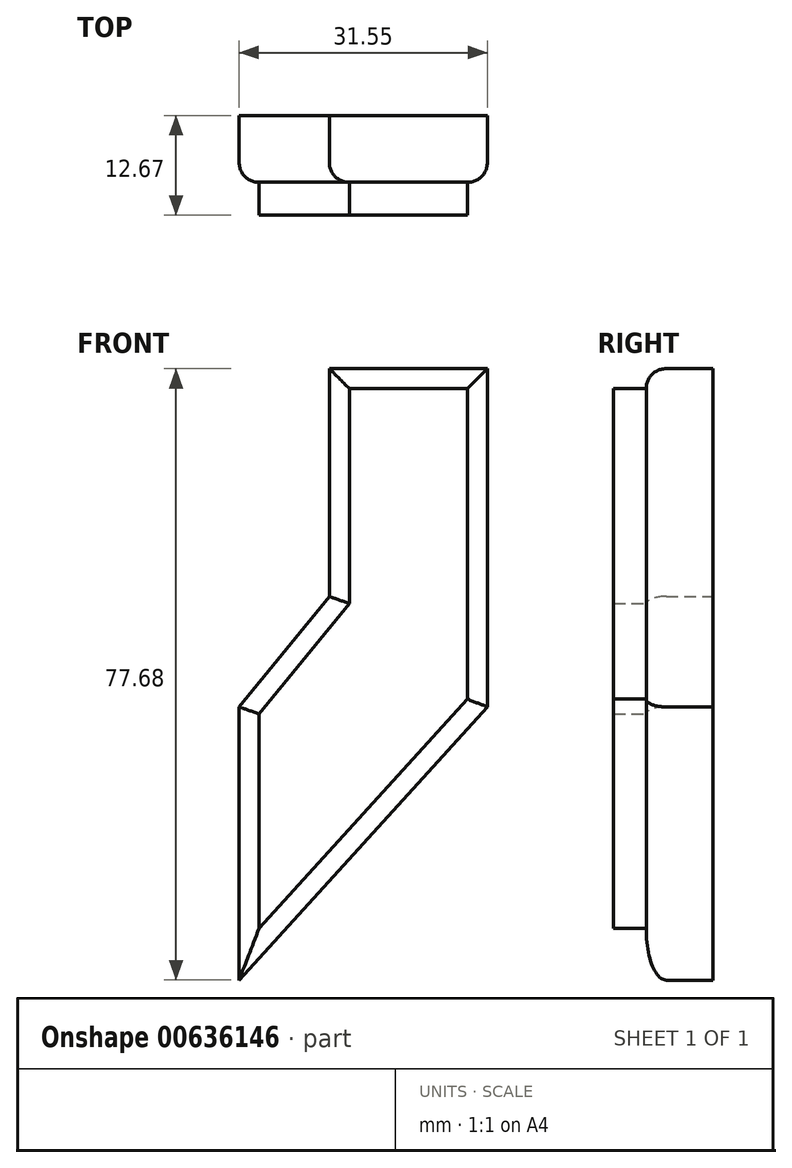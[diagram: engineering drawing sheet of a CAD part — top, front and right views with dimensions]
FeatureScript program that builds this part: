
annotation { "Feature Type Name" : "Feature", "Feature Type Description" : "" }
export const myFeature = defineFeature(function(context is Context, id is Id, definition is map)
    precondition{}
    {
        {
            var Q0;
            Q0=qCreatedBy(makeId("Front.planeOp"),FACE);
            var sketch = newSketch(context, id + "F0", { "sketchPlane" : qUnion([Q0])});
            skLineSegment(sketch, "E0", {"start": v(13.94, 0) * mm, "end": v(25.4, 14.03) * mm});
            skLineSegment(sketch, "E1", {"start": v(25.4, 14.03) * mm, "end": v(25.4, 42.97) * mm});
            skLineSegment(sketch, "E2", {"start": v(25.4, 42.97) * mm, "end": v(45.49, 42.97) * mm});
            skLineSegment(sketch, "E3", {"start": v(45.49, 42.97) * mm, "end": v(45.49, 0) * mm});
            skLineSegment(sketch, "E4", {"start": v(45.49, 0) * mm, "end": v(13.94, -34.71) * mm});
            skLineSegment(sketch, "E5", {"start": v(13.94, -34.71) * mm, "end": v(13.94, 0) * mm});
            skSolve(sketch);
        }
        {
            var Q0;
            Q0=makeQuery(id+"F0.imprint","IMPRINT",FACE,{"disambiguationData":[TD([[makeQuery(id+"F0.imprint","IMPRINT",EDGE,{"derivedFrom":sQuery(id+"F0.wireOp",EDGE,"E0")}),-1.0]])]});
            extrude(context, id + "F1", {"entities" : qUnion([Q0]), "endBound" : BoundingType.SYMMETRIC, "depth" : 8.5 * mm, "offsetDistance" : 25.4 * mm});
        }
        {
            var Q0;
            Q0=makeQuery(id+"F1.opExtrude","CAP_FACE",FACE,{"disambiguationData":[OSD([sQuery(id+"F0.wireOp",EDGE,"E0"),sQuery(id+"F0.wireOp",EDGE,"E1"),sQuery(id+"F0.wireOp",EDGE,"E2"),sQuery(id+"F0.wireOp",EDGE,"E3"),sQuery(id+"F0.wireOp",EDGE,"E4"),sQuery(id+"F0.wireOp",EDGE,"E5")])],"isStart":false});
            fillet(context, id + "F2", {"entities" : qUnion([Q0]), "radius" : 2.54 * mm, "tangentPropagation" : true, "allowEdgeOverflow" : false});
        }
        {
            var Q0;
            Q0=makeQuery(id+"F1.opExtrude","CAP_FACE",FACE,{"disambiguationData":[OSD([sQuery(id+"F0.wireOp",EDGE,"E0"),sQuery(id+"F0.wireOp",EDGE,"E1"),sQuery(id+"F0.wireOp",EDGE,"E2"),sQuery(id+"F0.wireOp",EDGE,"E3"),sQuery(id+"F0.wireOp",EDGE,"E4"),sQuery(id+"F0.wireOp",EDGE,"E5")])],"isStart":false});
            extrude(context, id + "F3", {"entities" : qUnion([Q0]), "operationType" : NewBodyOperationType.ADD, "depth" : 4.16 * mm, "offsetDistance" : 25.4 * mm});
        }
    });
